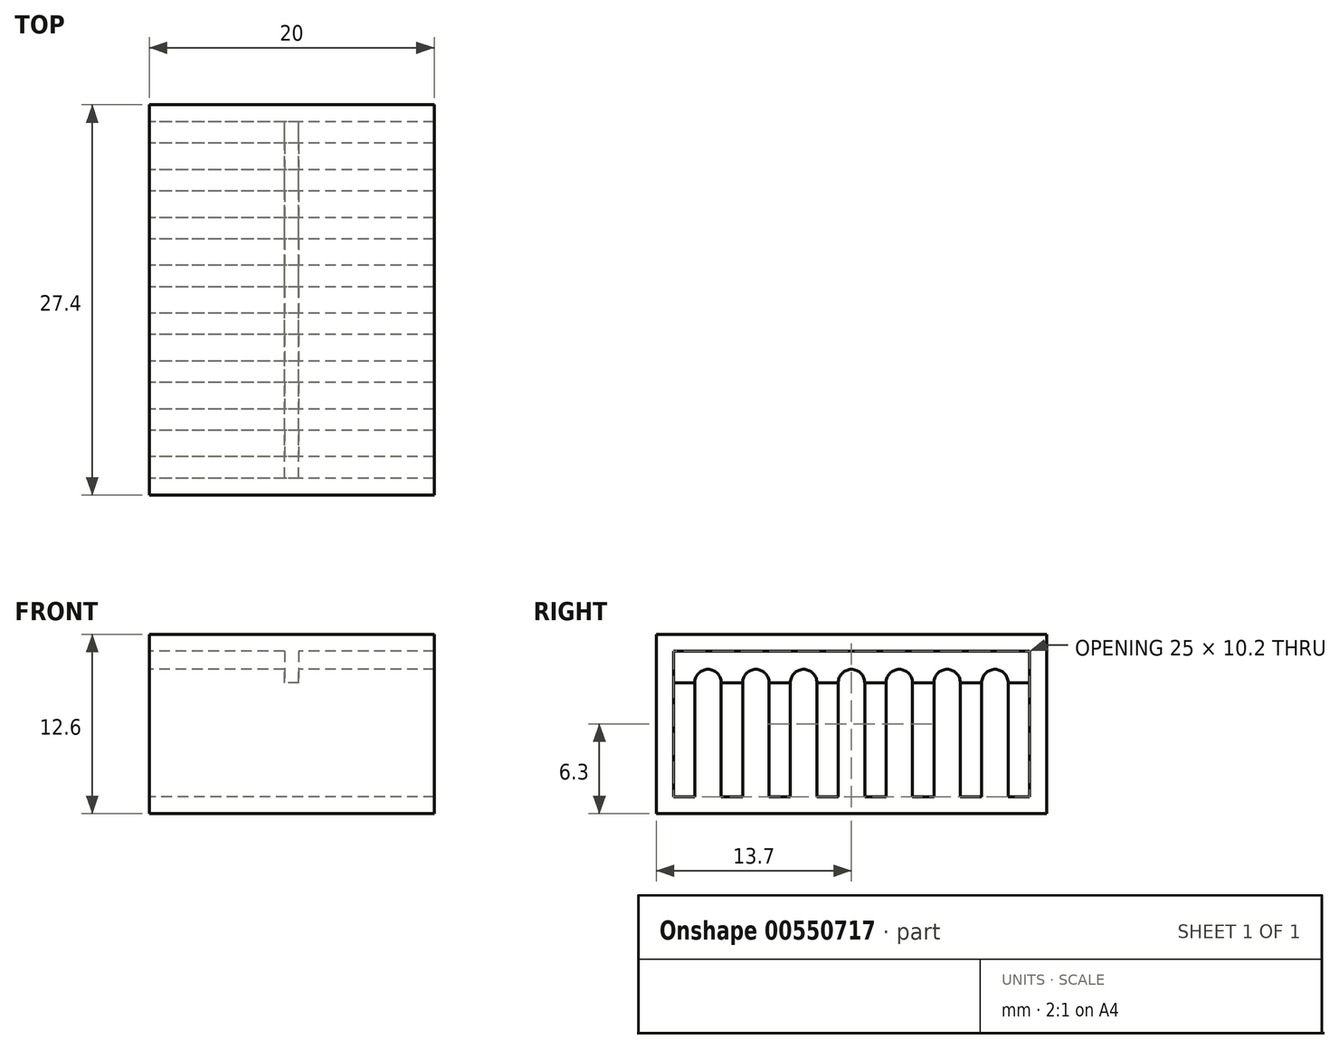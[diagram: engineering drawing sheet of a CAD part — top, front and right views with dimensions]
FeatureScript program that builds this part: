
annotation { "Feature Type Name" : "Feature", "Feature Type Description" : "" }
export const myFeature = defineFeature(function(context is Context, id is Id, definition is map)
    precondition{}
    {
        {
            var Q0;
            Q0=qCreatedBy(makeId("Right.planeOp"),FACE);
            var sketch = newSketch(context, id + "F0", { "sketchPlane" : qUnion([Q0])});
            skLineSegment(sketch, "E0.rect.bottom", {"start": v(-2.43, 4) * mm, "end": v(-0.93, 4) * mm});
            skLineSegment(sketch, "E0.rect.top", {"start": v(-2.43, -4) * mm, "end": v(-0.93, -4) * mm});
            skLineSegment(sketch, "E0.rect.left", {"start": v(-2.43, 4) * mm, "end": v(-2.43, -4) * mm});
            skLineSegment(sketch, "E0.rect.right", {"start": v(-0.93, 4) * mm, "end": v(-0.93, -4) * mm});
            skPoint(sketch, "E0.rect.middle", {"position": v(-1.68, 0) * mm});
            skLineSegment(sketch, "E1.rect.bottom", {"start": v(0.93, 4) * mm, "end": v(2.43, 4) * mm});
            skLineSegment(sketch, "E1.rect.top", {"start": v(0.93, -4) * mm, "end": v(2.43, -4) * mm});
            skLineSegment(sketch, "E1.rect.left", {"start": v(0.93, 4) * mm, "end": v(0.93, -4) * mm});
            skLineSegment(sketch, "E1.rect.right", {"start": v(2.43, 4) * mm, "end": v(2.43, -4) * mm});
            skPoint(sketch, "E1.rect.middle", {"position": v(1.68, 0) * mm});
            skLineSegment(sketch, "E2.rect.bottom", {"start": v(-5.79, 4) * mm, "end": v(-4.29, 4) * mm});
            skLineSegment(sketch, "E2.rect.top", {"start": v(-5.79, -4) * mm, "end": v(-4.29, -4) * mm});
            skLineSegment(sketch, "E2.rect.left", {"start": v(-5.79, 4) * mm, "end": v(-5.79, -4) * mm});
            skLineSegment(sketch, "E2.rect.right", {"start": v(-4.29, 4) * mm, "end": v(-4.29, -4) * mm});
            skPoint(sketch, "E2.rect.middle", {"position": v(-5.04, 0) * mm});
            skLineSegment(sketch, "E3.rect.bottom", {"start": v(-9.14, 4) * mm, "end": v(-7.64, 4) * mm});
            skLineSegment(sketch, "E3.rect.top", {"start": v(-9.14, -4) * mm, "end": v(-7.64, -4) * mm});
            skLineSegment(sketch, "E3.rect.left", {"start": v(-9.14, 4) * mm, "end": v(-9.14, -4) * mm});
            skLineSegment(sketch, "E3.rect.right", {"start": v(-7.64, 4) * mm, "end": v(-7.64, -4) * mm});
            skPoint(sketch, "E3.rect.middle", {"position": v(-8.4, 0) * mm});
            skLineSegment(sketch, "E4.rect.bottom", {"start": v(4.29, 4) * mm, "end": v(5.79, 4) * mm});
            skLineSegment(sketch, "E4.rect.top", {"start": v(4.29, -4) * mm, "end": v(5.79, -4) * mm});
            skLineSegment(sketch, "E4.rect.left", {"start": v(4.29, 4) * mm, "end": v(4.29, -4) * mm});
            skLineSegment(sketch, "E4.rect.right", {"start": v(5.79, 4) * mm, "end": v(5.79, -4) * mm});
            skPoint(sketch, "E4.rect.middle", {"position": v(5.04, 0) * mm});
            skLineSegment(sketch, "E5.rect.bottom", {"start": v(7.64, 4) * mm, "end": v(9.14, 4) * mm});
            skLineSegment(sketch, "E5.rect.top", {"start": v(7.64, -4) * mm, "end": v(9.14, -4) * mm});
            skLineSegment(sketch, "E5.rect.left", {"start": v(7.64, 4) * mm, "end": v(7.64, -4) * mm});
            skLineSegment(sketch, "E5.rect.right", {"start": v(9.14, 4) * mm, "end": v(9.14, -4) * mm});
            skPoint(sketch, "E5.rect.middle", {"position": v(8.4, 0) * mm});
            skLineSegment(sketch, "E6.rect.bottom", {"start": v(11, 4) * mm, "end": v(12.5, 4) * mm});
            skLineSegment(sketch, "E6.rect.top", {"start": v(11, -4) * mm, "end": v(12.5, -4) * mm});
            skLineSegment(sketch, "E6.rect.left", {"start": v(11, 4) * mm, "end": v(11, -4) * mm});
            skLineSegment(sketch, "E6.rect.right", {"start": v(12.5, 4) * mm, "end": v(12.5, -4) * mm});
            skPoint(sketch, "E6.rect.middle", {"position": v(11.75, 0) * mm});
            skLineSegment(sketch, "E7.rect.bottom", {"start": v(-12.5, 4) * mm, "end": v(-11, 4) * mm});
            skLineSegment(sketch, "E7.rect.top", {"start": v(-12.5, -4) * mm, "end": v(-11, -4) * mm});
            skLineSegment(sketch, "E7.rect.left", {"start": v(-12.5, 4) * mm, "end": v(-12.5, -4) * mm});
            skLineSegment(sketch, "E7.rect.right", {"start": v(-11, 4) * mm, "end": v(-11, -4) * mm});
            skPoint(sketch, "E7.rect.middle", {"position": v(-11.75, 0) * mm});
            skLineSegment(sketch, "E8", {"start": v(-11, -4) * mm, "end": v(-9.14, -4) * mm, "construction": true});
            skLineSegment(sketch, "E9", {"start": v(-7.64, -4) * mm, "end": v(-5.79, -4) * mm, "construction": true});
            skLineSegment(sketch, "E10", {"start": v(-4.29, -4) * mm, "end": v(-2.43, -4) * mm, "construction": true});
            skLineSegment(sketch, "E11", {"start": v(2.43, -4) * mm, "end": v(4.29, -4) * mm, "construction": true});
            skLineSegment(sketch, "E12", {"start": v(5.79, -4) * mm, "end": v(7.64, -4) * mm, "construction": true});
            skLineSegment(sketch, "E13", {"start": v(9.14, -4) * mm, "end": v(11, -4) * mm, "construction": true});
            skLineSegment(sketch, "E14", {"start": v(-0.93, -4) * mm, "end": v(0, -4) * mm, "construction": true});
            skLineSegment(sketch, "E15", {"start": v(0.93, -4) * mm, "end": v(0, -4) * mm, "construction": true});
            skArc(sketch, "E16", {"start": v(-2.43, 4) * mm, "mid": v(-3.36, 4.93) * mm, "end": v(-4.29, 4) * mm});
            skArc(sketch, "E17", {"start": v(-5.79, 4) * mm, "mid": v(-6.71, 4.93) * mm, "end": v(-7.64, 4) * mm});
            skArc(sketch, "E18", {"start": v(-9.14, 4) * mm, "mid": v(-10.07, 4.93) * mm, "end": v(-11, 4) * mm});
            skArc(sketch, "E19.0.MirrorCS", {"start": v(2.43, 4) * mm, "mid": v(3.36, 4.93) * mm, "end": v(4.29, 4) * mm});
            skArc(sketch, "E20.0.MirrorCS", {"start": v(5.79, 4) * mm, "mid": v(6.71, 4.93) * mm, "end": v(7.64, 4) * mm});
            skArc(sketch, "E21.0.MirrorCS", {"start": v(9.14, 4) * mm, "mid": v(10.07, 4.93) * mm, "end": v(11, 4) * mm});
            skLineSegment(sketch, "E22", {"start": v(-12.5, 4) * mm, "end": v(-12.5, 6.2) * mm});
            skLineSegment(sketch, "E23", {"start": v(-12.5, 6.2) * mm, "end": v(12.5, 6.2) * mm});
            skLineSegment(sketch, "E24", {"start": v(12.5, 6.2) * mm, "end": v(12.5, 4) * mm});
            skLineSegment(sketch, "E25", {"start": v(-10.07, 4.93) * mm, "end": v(10.07, 4.93) * mm, "construction": true});
            skArc(sketch, "E26", {"start": v(0.93, 4) * mm, "mid": v(0, 4.93) * mm, "end": v(-0.93, 4) * mm});
            skLineSegment(sketch, "E27", {"start": v(0, -11.15) * mm, "end": v(0, 14.13) * mm, "construction": true});
            skLineSegment(sketch, "E28", {"start": v(-12.5, 6.2) * mm, "end": v(12.5, -4) * mm, "construction": true});
            skLineSegment(sketch, "E29", {"start": v(-12.5, -4) * mm, "end": v(12.5, 6.2) * mm, "construction": true});
            skLineSegment(sketch, "E30.rect.bottom", {"start": v(-13.7, 7.4) * mm, "end": v(13.7, 7.4) * mm});
            skLineSegment(sketch, "E30.rect.top", {"start": v(-13.7, -5.2) * mm, "end": v(13.7, -5.2) * mm});
            skLineSegment(sketch, "E30.rect.left", {"start": v(-13.7, 7.4) * mm, "end": v(-13.7, -5.2) * mm});
            skLineSegment(sketch, "E30.rect.right", {"start": v(13.7, 7.4) * mm, "end": v(13.7, -5.2) * mm});
            skPoint(sketch, "E30.rect.middle", {"position": v(0, 1.1) * mm});
            skSolve(sketch);
        }
        {
            var Q0;
            Q0=makeQuery(id+"F0.imprint","IMPRINT",FACE,{"disambiguationData":[TD([[makeQuery(id+"F0.imprint","IMPRINT",EDGE,{"derivedFrom":sQuery(id+"F0.wireOp",EDGE,"E0.rect.top")}),-1.0]])]});
            var Q1;
            Q1=sQuery(id+"F0.wireOp",EDGE,"E28");
            extrude(context, id + "F1", {"entities" : qUnion([Q0]), "surfaceEntities" : qUnion([Q1]), "depth" : 20 * mm, "symmetric" : true});
        }
        {
            var Q0;
            Q0=qSketchRegion(id+"F0",true);
            var Q1;
            Q1=makeQuery(id+"F0.imprint","IMPRINT",FACE,{"disambiguationData":[TD([[makeQuery(id+"F0.imprint","IMPRINT",EDGE,{"derivedFrom":sQuery(id+"F0.wireOp",EDGE,"E0.rect.bottom")}),1.0]])]});
            extrude(context, id + "F2", {"entities" : qUnion([Q0, Q1]), "operationType" : NewBodyOperationType.ADD, "depth" : 1 * mm, "symmetric" : true});
        }
    });
